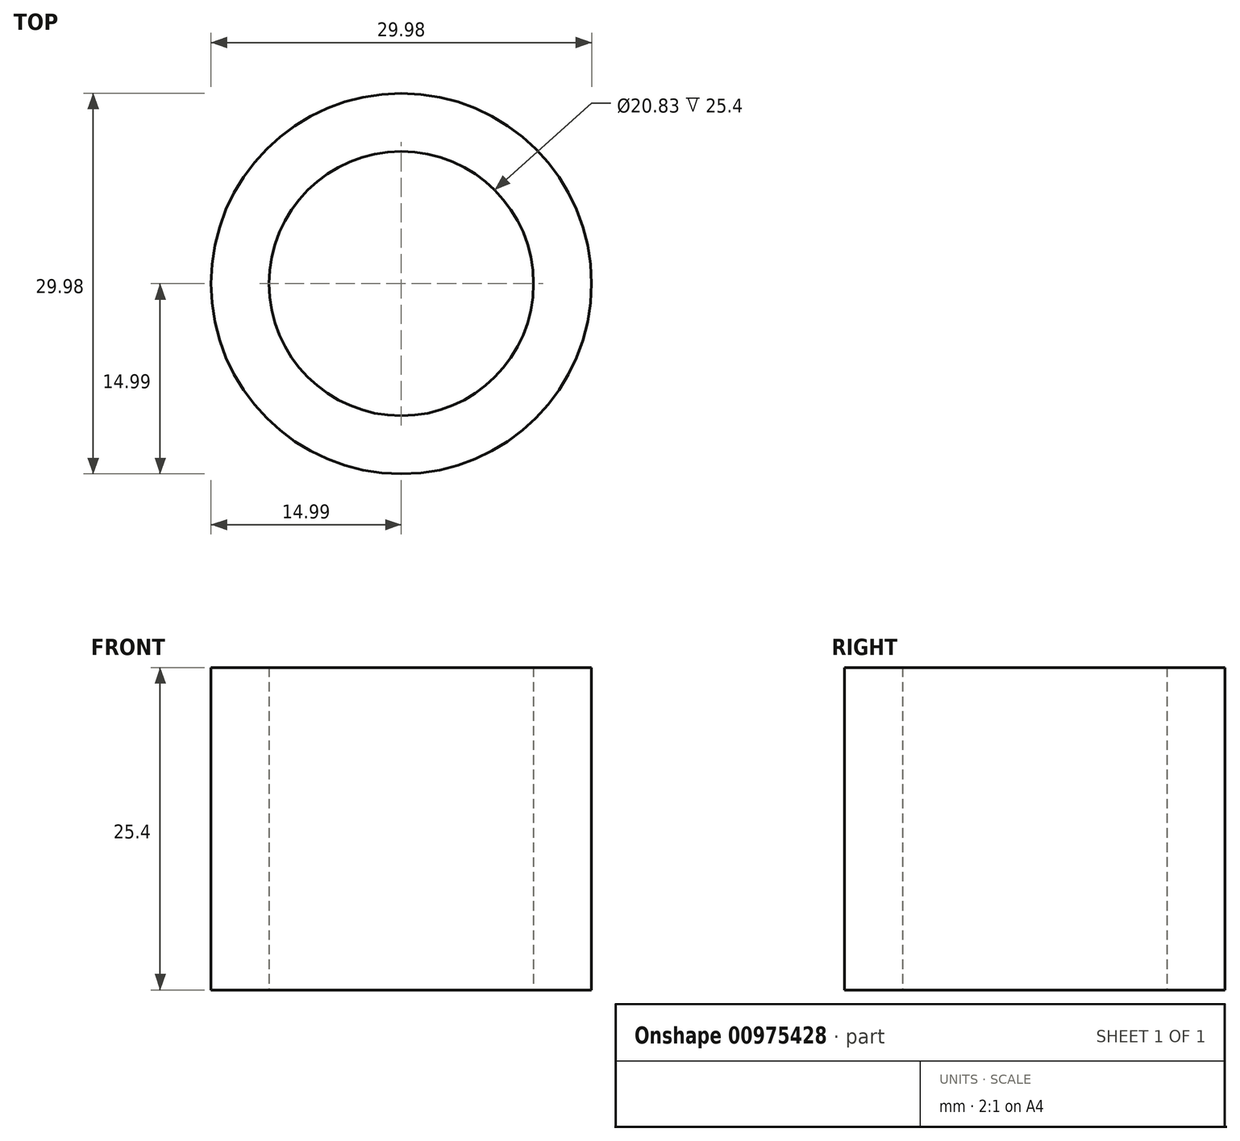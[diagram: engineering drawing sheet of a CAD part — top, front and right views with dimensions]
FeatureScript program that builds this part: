
annotation { "Feature Type Name" : "Feature", "Feature Type Description" : "" }
export const myFeature = defineFeature(function(context is Context, id is Id, definition is map)
    precondition{}
    {
        {
            var Q0;
            Q0=qCreatedBy(makeId("Top.planeOp"),FACE);
            var sketch = newSketch(context, id + "F0", { "sketchPlane" : qUnion([Q0])});
            skCircle(sketch, "E0", {"center": v(0, 0) * mm, "radius": 14.99 * mm});
            skCircle(sketch, "E1", {"center": v(0, 0) * mm, "radius": 10.41 * mm});
            skSolve(sketch);
        }
        {
            var Q0;
            Q0=makeQuery(id+"F0.imprint","IMPRINT",FACE,{"disambiguationData":[TD([[makeQuery(id+"F0.imprint","IMPRINT",EDGE,{"derivedFrom":sQuery(id+"F0.wireOp",EDGE,"E0")}),1.0]])]});
            extrude(context, id + "F1", {"entities" : qUnion([Q0]), "depth" : 25.4 * mm, "offsetDistance" : 25.4 * mm});
        }
    });
